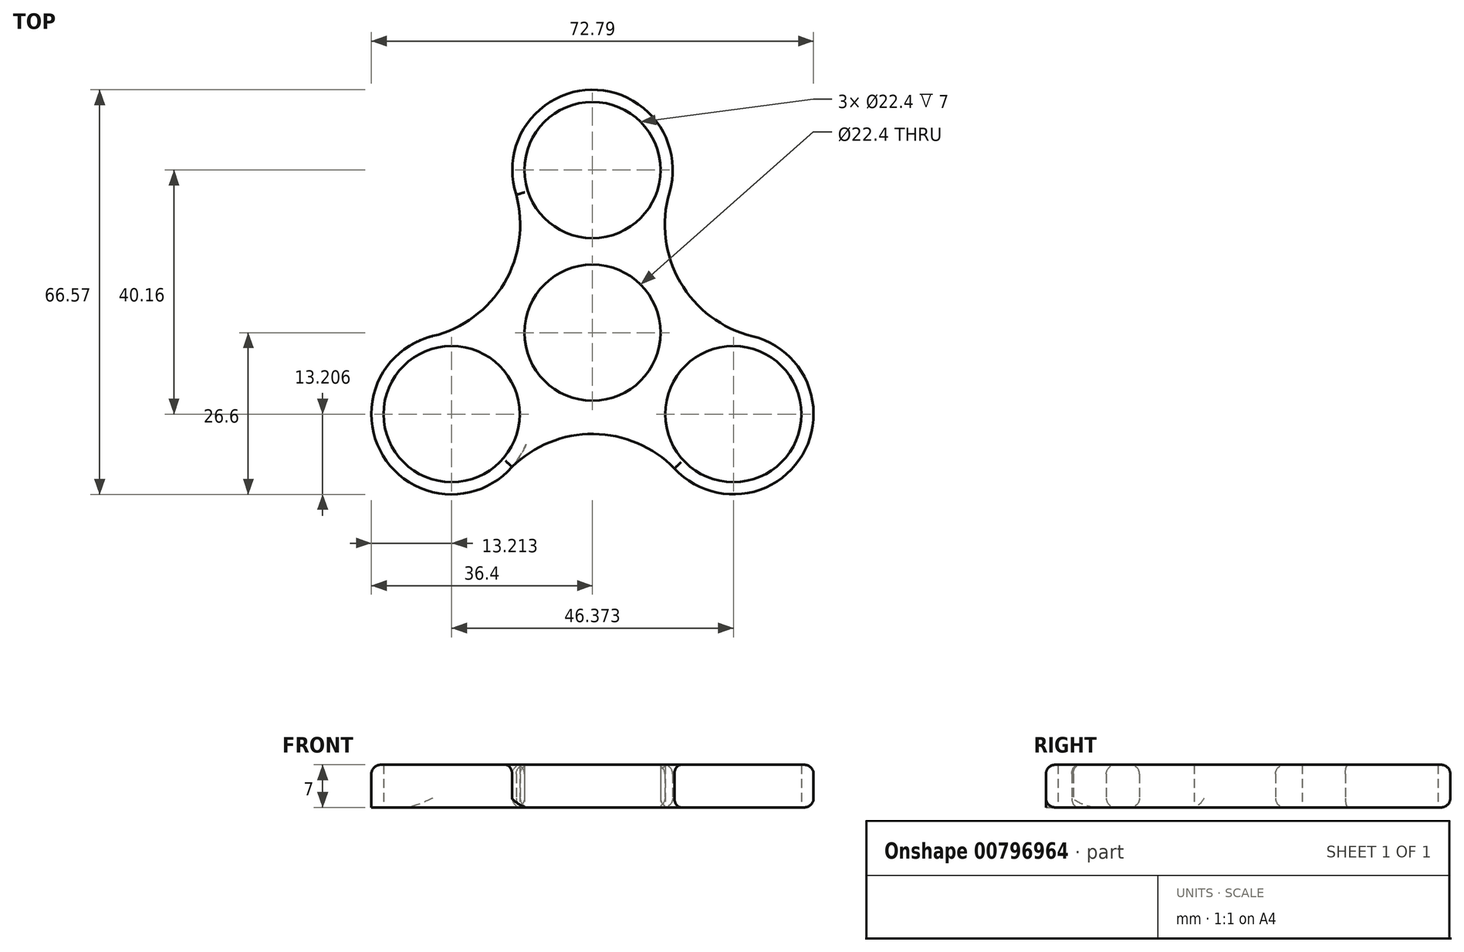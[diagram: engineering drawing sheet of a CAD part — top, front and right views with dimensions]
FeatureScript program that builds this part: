
annotation { "Feature Type Name" : "Feature", "Feature Type Description" : "" }
export const myFeature = defineFeature(function(context is Context, id is Id, definition is map)
    precondition{}
    {
        {
            var Q0;
            Q0=qCreatedBy(makeId("Top.planeOp"),FACE);
            var sketch = newSketch(context, id + "F0", { "sketchPlane" : qUnion([Q0])});
            skCircle(sketch, "E0", {"center": v(0, 0) * mm, "radius": 11.2 * mm});
            skCircle(sketch, "E1", {"center": v(0, 26.77) * mm, "radius": 11.2 * mm});
            skArc(sketch, "E2", {"start": v(12.67, 23.05) * mm, "mid": v(-0.19, 39.96) * mm, "end": v(-12.56, 22.7) * mm});
            skCircle(sketch, "E3.1.1", {"center": v(-23.19, -13.4) * mm, "radius": 11.2 * mm});
            skArc(sketch, "E3.2.0", {"start": v(13.48, -22.34) * mm, "mid": v(34.56, -20.1) * mm, "end": v(26.3, -0.57) * mm});
            skCircle(sketch, "E3.2.1", {"center": v(23.19, -13.4) * mm, "radius": 11.2 * mm});
            skArc(sketch, "E4", {"start": v(12.67, 23.05) * mm, "mid": v(14.43, 8.32) * mm, "end": v(26.3, -0.57) * mm});
            skArc(sketch, "E5.1.0", {"start": v(-26.3, -0.56) * mm, "mid": v(-14.43, 8.34) * mm, "end": v(-12.66, 23.06) * mm});
            skArc(sketch, "E5.2.0", {"start": v(13.63, -22.5) * mm, "mid": v(0, -16.66) * mm, "end": v(-13.64, -22.5) * mm});
            skArc(sketch, "E6", {"start": v(-26.3, -0.56) * mm, "mid": v(-34.48, -20.24) * mm, "end": v(-13.24, -22.09) * mm});
            skSolve(sketch);
        }
        {
            var Q0;
            Q0 = qSketchRegion(id + "F0", true);
            extrude(context, id + "F1", {"entities" : qUnion([Q0]), "depth" : 7 * mm, "offsetDistance" : 25 * mm});
        }
        {
            var Q0;
            Q0=makeQuery(id+"F1.opExtrude","CAP_EDGE",EDGE,{"disambiguationData":[OSD([sQuery(id+"F0.wireOp",EDGE,"E5.2.0")])],"isStart":false});
            var Q1;
            Q1=makeQuery(id+"F1.opExtrude","CAP_EDGE",EDGE,{"disambiguationData":[OSD([sQuery(id+"F0.wireOp",EDGE,"E5.1.0")])],"isStart":false});
            var Q2;
            Q2=makeQuery(id+"F1.opExtrude","CAP_EDGE",EDGE,{"disambiguationData":[OSD([sQuery(id+"F0.wireOp",EDGE,"E2")])],"isStart":false});
            fillet(context, id + "F2", {"entities" : qUnion([Q0, Q1, Q2]), "radius" : 1.5 * mm, "tangentPropagation" : true, "allowEdgeOverflow" : false});
        }
        {
            var Q0;
            Q0=makeQuery(id+"F1.opExtrude","CAP_EDGE",EDGE,{"disambiguationData":[OSD([sQuery(id+"F0.wireOp",EDGE,"E0")])],"isStart":false});
            var Q1;
            Q1=makeQuery(id+"F1.opExtrude","CAP_EDGE",EDGE,{"disambiguationData":[OSD([sQuery(id+"F0.wireOp",EDGE,"E2")])],"isStart":true});
            var Q2;
            Q2=makeQuery(id+"F1.opExtrude","CAP_EDGE",EDGE,{"disambiguationData":[OSD([sQuery(id+"F0.wireOp",EDGE,"E0")])],"isStart":true});
            fillet(context, id + "F3", {"entities" : qUnion([Q0, Q1, Q2]), "radius" : 1.5 * mm, "tangentPropagation" : true, "allowEdgeOverflow" : false});
        }
    });
